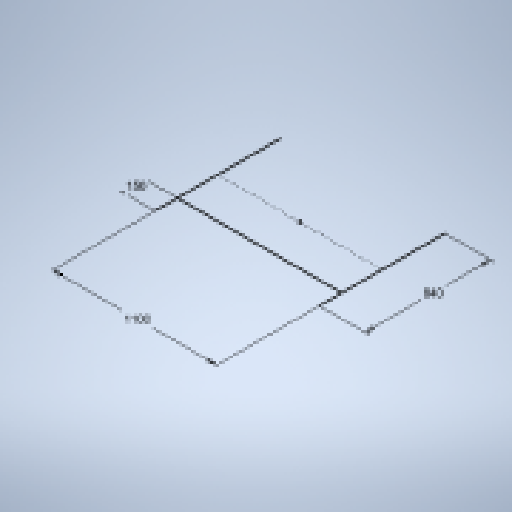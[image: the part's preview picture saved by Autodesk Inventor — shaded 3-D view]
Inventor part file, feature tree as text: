
AUTODESK INVENTOR PART (.ipt)
format: ipt  version: 2025 (Build 290162010, 162A)  size: 129,024 bytes
history: native  units: mm
features: sketch x1
ambient origin geometry x8: Origin, YZ Plane, XZ Plane, XY Plane, X Axis, Y Axis, Z Axis, Center Point
feature tree (1):
  sketch  "Sketch1"  dims[d0=1100.0mm d1=840.0mm d2=150.0mm]
